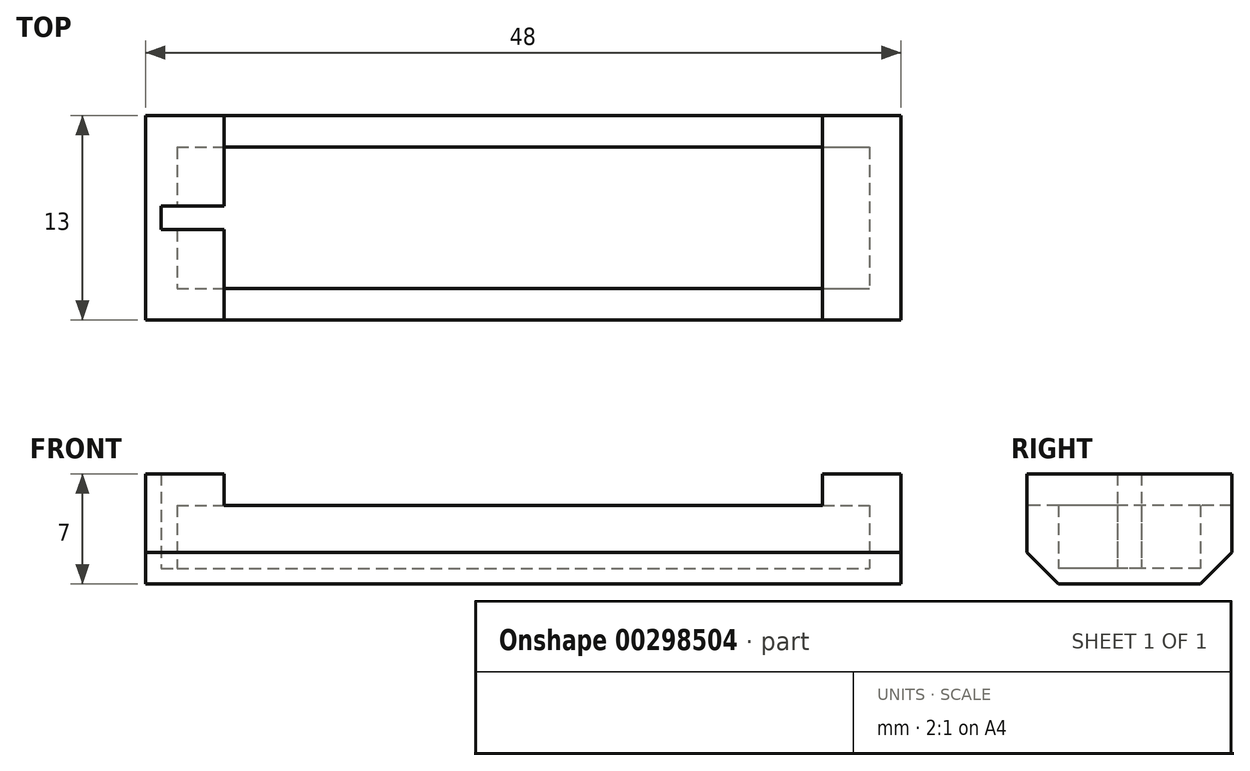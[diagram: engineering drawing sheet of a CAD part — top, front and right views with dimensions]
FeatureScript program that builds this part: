
annotation { "Feature Type Name" : "Feature", "Feature Type Description" : "" }
export const myFeature = defineFeature(function(context is Context, id is Id, definition is map)
    precondition{}
    {
        {
            var Q0;
            Q0=qCreatedBy(makeId("Top.planeOp"),FACE);
            var sketch = newSketch(context, id + "F0", { "sketchPlane" : qUnion([Q0])});
            skLineSegment(sketch, "E0.bottom", {"start": v(-22, 4.5) * mm, "end": v(22, 4.5) * mm});
            skLineSegment(sketch, "E0.top", {"start": v(-22, -4.5) * mm, "end": v(22, -4.5) * mm});
            skLineSegment(sketch, "E0.left", {"start": v(-22, 4.5) * mm, "end": v(-22, -4.5) * mm});
            skLineSegment(sketch, "E0.right", {"start": v(22, 4.5) * mm, "end": v(22, -4.5) * mm});
            skPoint(sketch, "E0.middle", {"position": v(0, 0) * mm});
            skLineSegment(sketch, "E1.0", {"start": v(-24, -6.5) * mm, "end": v(24, -6.5) * mm});
            skLineSegment(sketch, "E1.1", {"start": v(-24, 6.5) * mm, "end": v(-24, -6.5) * mm});
            skLineSegment(sketch, "E1.2", {"start": v(-24, 6.5) * mm, "end": v(24, 6.5) * mm});
            skLineSegment(sketch, "E1.3", {"start": v(24, 6.5) * mm, "end": v(24, -6.5) * mm});
            skSolve(sketch);
        }
        {
            var Q0;
            Q0=makeQuery(id+"F0.imprint","IMPRINT",FACE,{"disambiguationData":[TD([[makeQuery(id+"F0.imprint","IMPRINT",EDGE,{"derivedFrom":sQuery(id+"F0.wireOp",EDGE,"E0.bottom")}),1.0]])]});
            extrude(context, id + "F1", {"entities" : qUnion([Q0]), "depth" : 4 * mm});
        }
        {
            var Q0;
            Q0=makeQuery(id+"F0.imprint","IMPRINT",FACE,{"disambiguationData":[TD([[makeQuery(id+"F0.imprint","IMPRINT",EDGE,{"derivedFrom":sQuery(id+"F0.wireOp",EDGE,"E0.bottom")}),-1.0]])]});
            var Q1;
            Q1=makeQuery(id+"F0.imprint","IMPRINT",FACE,{"disambiguationData":[TD([[makeQuery(id+"F0.imprint","IMPRINT",EDGE,{"derivedFrom":sQuery(id+"F0.wireOp",EDGE,"E0.bottom")}),1.0]])]});
            extrude(context, id + "F2", {"entities" : qUnion([Q0, Q1]), "operationType" : NewBodyOperationType.ADD, "oppositeDirection" : true, "depth" : 1 * mm});
        }
        {
            var Q0;
            Q0=makeQuery(id+"F1.opExtrude","CAP_FACE",FACE,{"disambiguationData":[OSD([sQuery(id+"F0.wireOp",EDGE,"E0.bottom"),sQuery(id+"F0.wireOp",EDGE,"E0.top"),sQuery(id+"F0.wireOp",EDGE,"E0.left"),sQuery(id+"F0.wireOp",EDGE,"E0.right"),sQuery(id+"F0.wireOp",EDGE,"E1.0"),sQuery(id+"F0.wireOp",EDGE,"E1.1"),sQuery(id+"F0.wireOp",EDGE,"E1.2"),sQuery(id+"F0.wireOp",EDGE,"E1.3")])],"isStart":false});
            var sketch = newSketch(context, id + "F3", { "sketchPlane" : qUnion([Q0])});
            skLineSegment(sketch, "E2", {"start": v(-19, 6.5) * mm, "end": v(-19, -6.5) * mm});
            skLineSegment(sketch, "E3", {"start": v(0, -6.5) * mm, "end": v(0, 6.5) * mm, "construction": true});
            skLineSegment(sketch, "E4", {"start": v(19, 6.5) * mm, "end": v(19, -6.5) * mm});
            skSolve(sketch);
        }
        {
            var Q0;
            Q0=qSketchRegion(id+"F3",true);
            var Q1;
            {var subQ1=makeQuery(id+"F1.opExtrude","CAP_EDGE",EDGE,{"disambiguationData":[OSD([sQuery(id+"F0.wireOp",EDGE,"E0.left")])],"isStart":false});Q1=makeQuery(id+"F3.imprint","IMPRINT",FACE,{"disambiguationData":[TD([[makeQuery(id+"F3.imprint","IMPRINT",EDGE,{"derivedFrom":subQ1}),-1.0]])]});}
            var Q2;
            {var subQ5=makeQuery(id+"F1.opExtrude","CAP_EDGE",EDGE,{"disambiguationData":[OSD([sQuery(id+"F0.wireOp",EDGE,"E0.left")])],"isStart":false});Q2=makeQuery(id+"F3.imprint","IMPRINT",FACE,{"disambiguationData":[TD([[makeQuery(id+"F3.imprint","IMPRINT",EDGE,{"derivedFrom":subQ5}),1.0]])]});}
            var Q3;
            {var subQ6=makeQuery(id+"F1.opExtrude","CAP_EDGE",EDGE,{"disambiguationData":[OSD([sQuery(id+"F0.wireOp",EDGE,"E0.right")])],"isStart":false});Q3=makeQuery(id+"F3.imprint","IMPRINT",FACE,{"disambiguationData":[TD([[makeQuery(id+"F3.imprint","IMPRINT",EDGE,{"derivedFrom":subQ6}),1.0]])]});}
            var Q4;
            {var subQ5=makeQuery(id+"F1.opExtrude","CAP_EDGE",EDGE,{"disambiguationData":[OSD([sQuery(id+"F0.wireOp",EDGE,"E0.right")])],"isStart":false});Q4=makeQuery(id+"F3.imprint","IMPRINT",FACE,{"disambiguationData":[TD([[makeQuery(id+"F3.imprint","IMPRINT",EDGE,{"derivedFrom":subQ5}),-1.0]])]});}
            extrude(context, id + "F4", {"entities" : qUnion([Q0, Q1, Q2, Q3, Q4]), "operationType" : NewBodyOperationType.ADD, "depth" : 2 * mm});
        }
        {
            var Q0;
            Q0=makeQuery(id+"F2.opExtrude","CAP_EDGE",EDGE,{"disambiguationData":[OSD([sQuery(id+"F0.wireOp",EDGE,"E1.0")])],"isStart":false});
            var Q1;
            Q1=makeQuery(id+"F2.opExtrude","CAP_EDGE",EDGE,{"disambiguationData":[OSD([sQuery(id+"F0.wireOp",EDGE,"E1.2")])],"isStart":false});
            chamfer(context, id + "F5", {"entities" : qUnion([Q0, Q1]), "width" : 2 * mm, "tangentPropagation" : true});
        }
        {
            var Q0;
            Q0=makeQuery(id+"F4.opExtrude","SWEPT_FACE",FACE,{"disambiguationData":[OSD([sQuery(id+"F3.wireOp",EDGE,"E2")])]});
            var sketch = newSketch(context, id + "F6", { "sketchPlane" : qUnion([Q0])});
            skLineSegment(sketch, "E5.bottom", {"start": v(0.75, 6) * mm, "end": v(-0.75, 6) * mm});
            skLineSegment(sketch, "E5.top", {"start": v(0.75, 0) * mm, "end": v(-0.75, 0) * mm});
            skLineSegment(sketch, "E5.left", {"start": v(0.75, 6) * mm, "end": v(0.75, 0) * mm});
            skLineSegment(sketch, "E5.right", {"start": v(-0.75, 6) * mm, "end": v(-0.75, 0) * mm});
            skPoint(sketch, "E5.middle", {"position": v(0, 3) * mm});
            skSolve(sketch);
        }
        {
            var Q0;
            Q0=qSketchRegion(id+"F6",true);
            extrude(context, id + "F7", {"entities" : qUnion([Q0]), "operationType" : NewBodyOperationType.REMOVE, "oppositeDirection" : true, "depth" : 4 * mm});
        }
    });
